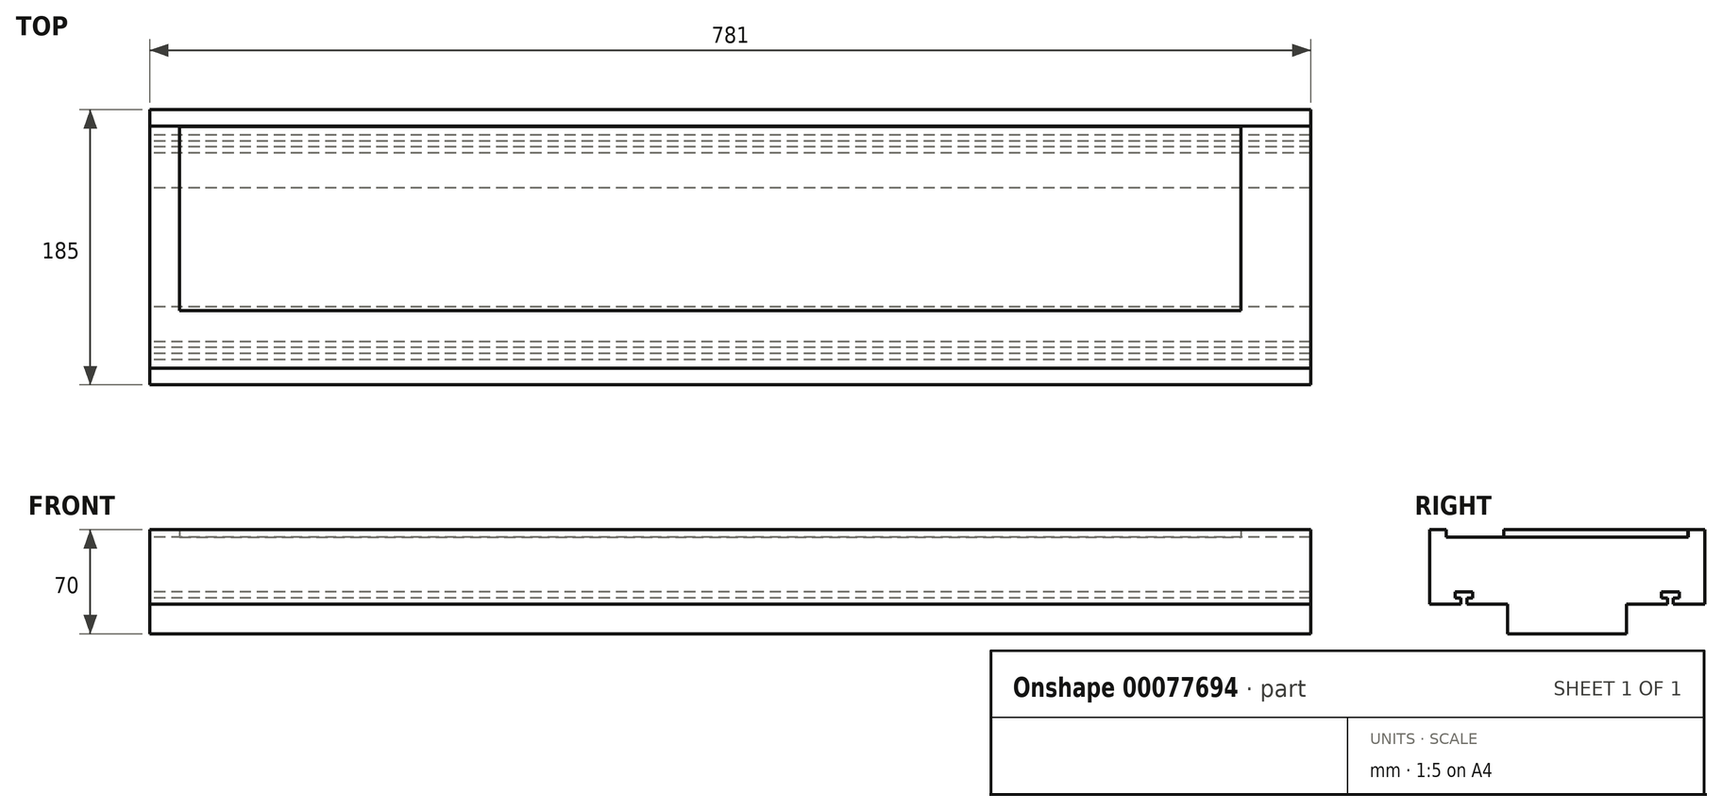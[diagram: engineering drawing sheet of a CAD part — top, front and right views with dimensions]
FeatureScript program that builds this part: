
annotation { "Feature Type Name" : "Feature", "Feature Type Description" : "" }
export const myFeature = defineFeature(function(context is Context, id is Id, definition is map)
    precondition{}
    {
        {
            var Q0;
            Q0=qCreatedBy(makeId("Right.planeOp"),FACE);
            var sketch = newSketch(context, id + "F0", { "sketchPlane" : qUnion([Q0])});
            skLineSegment(sketch, "E0", {"start": v(-92.5, 0) * mm, "end": v(92.5, 0) * mm, "construction": true});
            skLineSegment(sketch, "E1.bottom", {"start": v(-92.5, 0) * mm, "end": v(-71.5, 0) * mm});
            skLineSegment(sketch, "E1.top", {"start": v(-92.5, 50) * mm, "end": v(92.5, 50) * mm});
            skLineSegment(sketch, "E1.left", {"start": v(-92.5, 0) * mm, "end": v(-92.5, 50) * mm});
            skLineSegment(sketch, "E1.right", {"start": v(92.5, 0) * mm, "end": v(92.5, 50) * mm});
            skLineSegment(sketch, "E2", {"start": v(0, 0) * mm, "end": v(0, -20) * mm, "construction": true});
            skLineSegment(sketch, "E3", {"start": v(0, -20) * mm, "end": v(-40, -20) * mm, "construction": true});
            skLineSegment(sketch, "E4.bottom", {"start": v(-40, -20) * mm, "end": v(40, -20) * mm});
            skLineSegment(sketch, "E4.top", {"start": v(-40, 0) * mm, "end": v(40, 0) * mm});
            skLineSegment(sketch, "E4.left", {"start": v(-40, -20) * mm, "end": v(-40, 0) * mm});
            skLineSegment(sketch, "E4.right", {"start": v(40, -20) * mm, "end": v(40, 0) * mm});
            skLineSegment(sketch, "E5", {"start": v(0, 85.73) * mm, "end": v(0, -82.56) * mm, "construction": true});
            skLineSegment(sketch, "E6.0", {"start": v(-67.5, 85.73) * mm, "end": v(-67.5, 50) * mm, "construction": true});
            skLineSegment(sketch, "E7.0", {"start": v(-71.5, 85.73) * mm, "end": v(-71.5, 50) * mm, "construction": true});
            skLineSegment(sketch, "E8.0", {"start": v(-63.5, 85.73) * mm, "end": v(-63.5, 50) * mm, "construction": true});
            skLineSegment(sketch, "E9.0", {"start": v(-75.5, 4) * mm, "end": v(-71.5, 4) * mm});
            skLineSegment(sketch, "E10.0", {"start": v(-75.5, 85.73) * mm, "end": v(-75.5, 50) * mm, "construction": true});
            skLineSegment(sketch, "E11.0", {"start": v(-75.5, 8) * mm, "end": v(-63.5, 8) * mm});
            skLineSegment(sketch, "E12.trimOffspring", {"start": v(0, 8) * mm, "end": v(92.5, 8) * mm, "construction": true});
            skLineSegment(sketch, "E13.trimOffspring", {"start": v(0, 4) * mm, "end": v(92.5, 4) * mm, "construction": true});
            skLineSegment(sketch, "E14.trimOffspring", {"start": v(-63.5, 8) * mm, "end": v(-63.5, 4) * mm, "construction": true});
            skLineSegment(sketch, "E15.trimOffspring", {"start": v(-67.5, 4) * mm, "end": v(-67.5, -82.56) * mm, "construction": true});
            skLineSegment(sketch, "E16.trimOffspring", {"start": v(-71.5, 4) * mm, "end": v(-71.5, -82.56) * mm, "construction": true});
            skLineSegment(sketch, "E17.trimOffspring", {"start": v(-75.5, 8) * mm, "end": v(-75.5, 4) * mm, "construction": true});
            skLineSegment(sketch, "E18.trimOffspring", {"start": v(-75.5, 0) * mm, "end": v(-75.5, -82.56) * mm, "construction": true});
            skLineSegment(sketch, "E19.trimOffspring", {"start": v(-63.5, 0) * mm, "end": v(-63.5, -82.56) * mm, "construction": true});
            skLineSegment(sketch, "E20.trimOffspring", {"start": v(-67.5, 4) * mm, "end": v(-63.5, 4) * mm});
            skLineSegment(sketch, "E21.trimOffspring", {"start": v(-67.5, 0) * mm, "end": v(67.5, 0) * mm});
            skLineSegment(sketch, "E22", {"start": v(-71.5, 0) * mm, "end": v(-71.5, 4) * mm});
            skLineSegment(sketch, "E23", {"start": v(-75.5, 4) * mm, "end": v(-75.5, 8) * mm});
            skLineSegment(sketch, "E24", {"start": v(-63.5, 8) * mm, "end": v(-63.5, 4) * mm});
            skLineSegment(sketch, "E25", {"start": v(-67.5, 4) * mm, "end": v(-67.5, 0) * mm});
            skLineSegment(sketch, "E26.MirrorCS", {"start": v(67.5, 4) * mm, "end": v(63.5, 4) * mm});
            skLineSegment(sketch, "E27.MirrorCS", {"start": v(75.5, 4) * mm, "end": v(71.5, 4) * mm});
            skLineSegment(sketch, "E28.MirrorCS", {"start": v(67.5, 4) * mm, "end": v(67.5, 0) * mm});
            skLineSegment(sketch, "E29.MirrorCS", {"start": v(63.5, 8) * mm, "end": v(63.5, 4) * mm, "construction": true});
            skLineSegment(sketch, "E30.MirrorCS", {"start": v(75.5, 8) * mm, "end": v(75.5, 4) * mm, "construction": true});
            skLineSegment(sketch, "E31.MirrorCS", {"start": v(75.5, 4) * mm, "end": v(75.5, 8) * mm});
            skLineSegment(sketch, "E32.MirrorCS", {"start": v(71.5, 0) * mm, "end": v(71.5, 4) * mm});
            skLineSegment(sketch, "E33.MirrorCS", {"start": v(63.5, 8) * mm, "end": v(63.5, 4) * mm});
            skLineSegment(sketch, "E34.MirrorCS", {"start": v(75.5, 8) * mm, "end": v(63.5, 8) * mm});
            skLineSegment(sketch, "E35.trimOffspring", {"start": v(71.5, 0) * mm, "end": v(92.5, 0) * mm});
            skSolve(sketch);
        }
        {
            var Q0;
            Q0 = qSketchRegion(id + "F0", true);
            extrude(context, id + "F1", {"entities" : qUnion([Q0]), "endBound" : BoundingType.SYMMETRIC, "depth" : 781 * mm});
        }
        {
            var Q0;
            Q0=makeQuery(id+"F1.opExtrude","SWEPT_FACE",FACE,{"disambiguationData":[OSD([sQuery(id+"F0.wireOp",EDGE,"E1.top")])]});
            var sketch = newSketch(context, id + "F2", { "sketchPlane" : qUnion([Q0])});
            skLineSegment(sketch, "E36.0", {"start": v(390.5, 81.5) * mm, "end": v(-390.5, 81.5) * mm});
            skLineSegment(sketch, "E37.0", {"start": v(390.5, -81.5) * mm, "end": v(-390.5, -81.5) * mm});
            skLineSegment(sketch, "E38.0", {"start": v(-390.5, -92.5) * mm, "end": v(-390.5, 92.5) * mm});
            skLineSegment(sketch, "E39.0", {"start": v(390.5, -92.5) * mm, "end": v(390.5, 92.5) * mm});
            skSolve(sketch);
        }
        {
            var Q0;
            Q0 = qSketchRegion(id + "F2", true);
            extrude(context, id + "F3", {"entities" : qUnion([Q0]), "operationType" : NewBodyOperationType.REMOVE, "oppositeDirection" : true, "depth" : 5 * mm});
        }
        {
            var Q0;
            Q0=makeQuery(id+"F3.boolean.opBoolean","COPY",FACE,{"derivedFrom":makeQuery(id+"F3.opExtrude","CAP_FACE",FACE,{"disambiguationData":[OSD([sQuery(id+"F2.wireOp",EDGE,"E36.0"),sQuery(id+"F2.wireOp",EDGE,"E37.0"),sQuery(id+"F2.wireOp",EDGE,"E38.0"),sQuery(id+"F2.wireOp",EDGE,"E39.0")])],"isStart":false})});
            var sketch = newSketch(context, id + "F4", { "sketchPlane" : qUnion([Q0])});
            skLineSegment(sketch, "E40.bottom", {"start": v(-370.5, 81.3) * mm, "end": v(343.5, 81.3) * mm});
            skLineSegment(sketch, "E40.top", {"start": v(-370.5, -42.7) * mm, "end": v(343.5, -42.7) * mm});
            skLineSegment(sketch, "E40.left", {"start": v(-370.5, 81.3) * mm, "end": v(-370.5, -42.7) * mm});
            skLineSegment(sketch, "E40.right", {"start": v(343.5, 81.3) * mm, "end": v(343.5, -42.7) * mm});
            skSolve(sketch);
        }
        {
            var Q0;
            Q0 = qSketchRegion(id + "F4", true);
            extrude(context, id + "F5", {"entities" : qUnion([Q0]), "operationType" : NewBodyOperationType.ADD, "depth" : 5 * mm});
        }
    });
